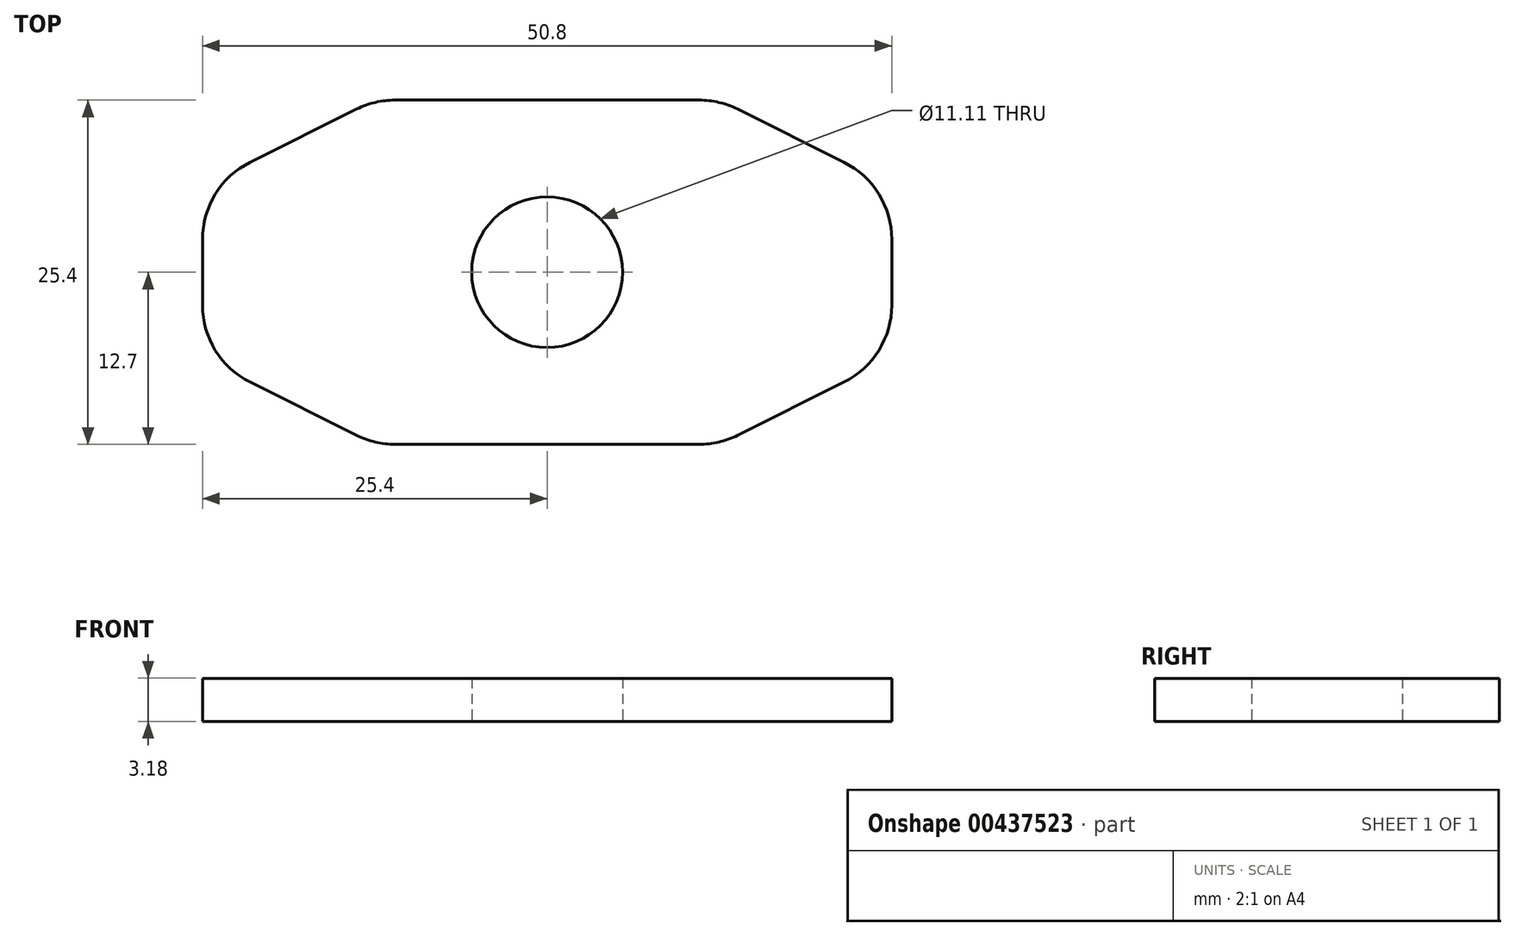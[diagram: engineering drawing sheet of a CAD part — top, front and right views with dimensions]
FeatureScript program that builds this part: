
annotation { "Feature Type Name" : "Feature", "Feature Type Description" : "" }
export const myFeature = defineFeature(function(context is Context, id is Id, definition is map)
    precondition{}
    {
        {
            var Q0;
            Q0=qCreatedBy(makeId("Top.planeOp"),FACE);
            var sketch = newSketch(context, id + "F0", { "sketchPlane" : qUnion([Q0])});
            skLineSegment(sketch, "E0", {"start": v(-25.4, 6.35) * mm, "end": v(-25.4, -6.35) * mm});
            skLineSegment(sketch, "E1", {"start": v(-25.4, -6.35) * mm, "end": v(-12.7, -12.7) * mm});
            skLineSegment(sketch, "E2", {"start": v(-12.7, -12.7) * mm, "end": v(12.7, -12.7) * mm});
            skLineSegment(sketch, "E3", {"start": v(12.7, -12.7) * mm, "end": v(25.4, -6.35) * mm});
            skLineSegment(sketch, "E4", {"start": v(25.4, -6.35) * mm, "end": v(25.4, 6.35) * mm});
            skLineSegment(sketch, "E5", {"start": v(25.4, 6.35) * mm, "end": v(12.7, 12.7) * mm});
            skLineSegment(sketch, "E6", {"start": v(12.7, 12.7) * mm, "end": v(-12.7, 12.7) * mm});
            skLineSegment(sketch, "E7", {"start": v(-12.7, 12.7) * mm, "end": v(-25.4, 6.35) * mm});
            skLineSegment(sketch, "E8", {"start": v(0, 12.7) * mm, "end": v(0, -12.7) * mm, "construction": true});
            skLineSegment(sketch, "E9", {"start": v(-25.4, 0) * mm, "end": v(25.4, 0) * mm, "construction": true});
            skCircle(sketch, "E10", {"center": v(0, 0) * mm, "radius": 5.56 * mm});
            skSolve(sketch);
        }
        {
            var Q0;
            Q0=makeQuery(id+"F0.imprint","IMPRINT",FACE,{"disambiguationData":[TD([[makeQuery(id+"F0.imprint","IMPRINT",EDGE,{"derivedFrom":sQuery(id+"F0.wireOp",EDGE,"E0")}),1.0]])]});
            extrude(context, id + "F1", {"entities" : qUnion([Q0]), "depth" : 3.17 * mm});
        }
        {
            var Q0;
            Q0=makeQuery(id+"F1.opExtrude","SWEPT_EDGE",EDGE,{"disambiguationData":[OSD([sQuery(id+"F0.wireOp",EDGE,"E1"),sQuery(id+"F0.wireOp",EDGE,"E2")])]});
            var Q1;
            Q1=makeQuery(id+"F1.opExtrude","SWEPT_EDGE",EDGE,{"disambiguationData":[OSD([sQuery(id+"F0.wireOp",EDGE,"E2"),sQuery(id+"F0.wireOp",EDGE,"E3")])]});
            var Q2;
            Q2=makeQuery(id+"F1.opExtrude","SWEPT_EDGE",EDGE,{"disambiguationData":[OSD([sQuery(id+"F0.wireOp",EDGE,"E3"),sQuery(id+"F0.wireOp",EDGE,"E4")])]});
            var Q3;
            Q3=makeQuery(id+"F1.opExtrude","SWEPT_EDGE",EDGE,{"disambiguationData":[OSD([sQuery(id+"F0.wireOp",EDGE,"E4"),sQuery(id+"F0.wireOp",EDGE,"E5")])]});
            var Q4;
            Q4=makeQuery(id+"F1.opExtrude","SWEPT_EDGE",EDGE,{"disambiguationData":[OSD([sQuery(id+"F0.wireOp",EDGE,"E5"),sQuery(id+"F0.wireOp",EDGE,"E6")])]});
            var Q5;
            Q5=makeQuery(id+"F1.opExtrude","SWEPT_EDGE",EDGE,{"disambiguationData":[OSD([sQuery(id+"F0.wireOp",EDGE,"E6"),sQuery(id+"F0.wireOp",EDGE,"E7")])]});
            var Q6;
            Q6=makeQuery(id+"F1.opExtrude","SWEPT_EDGE",EDGE,{"disambiguationData":[OSD([sQuery(id+"F0.wireOp",EDGE,"E0"),sQuery(id+"F0.wireOp",EDGE,"E7")])]});
            var Q7;
            Q7=makeQuery(id+"F1.opExtrude","SWEPT_EDGE",EDGE,{"disambiguationData":[OSD([sQuery(id+"F0.wireOp",EDGE,"E0"),sQuery(id+"F0.wireOp",EDGE,"E1")])]});
            fillet(context, id + "F2", {"entities" : qUnion([Q0, Q1, Q2, Q3, Q4, Q5, Q6, Q7]), "radius" : 6.35 * mm, "tangentPropagation" : true, "allowEdgeOverflow" : false});
        }
    });
